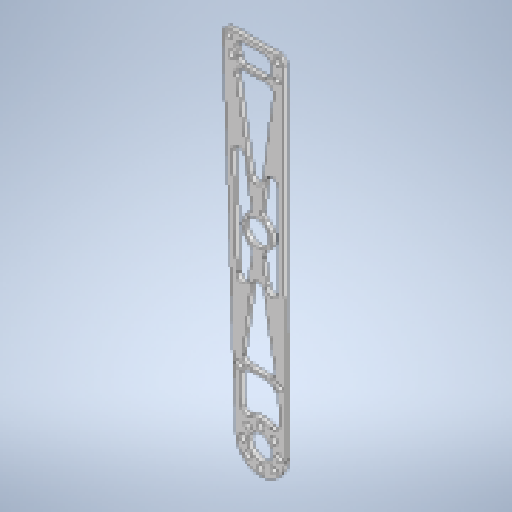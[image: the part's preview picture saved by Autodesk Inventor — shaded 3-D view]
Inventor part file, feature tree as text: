
AUTODESK INVENTOR PART (.ipt)
format: ipt  version: 2025.1 (Build 291241000, 241)  size: 314,880 bytes
history: native  units: mm
features: reference x12, other x8, extrude x2, fillet x2, sketch x2
ambient origin geometry x8: Origin, YZ Plane, XZ Plane, XY Plane, X Axis, Y Axis, Z Axis, Center Point
bodies: Body1 (feature_tree)
feature tree (26):
  other  "ソリッド1"
  extrude  "押し出し1"  Depth=8.0mm
  fillet  "フィレット1"  Radius=16.0mm
  extrude  "押し出し2"  Depth=12.0mm
  fillet  "フィレット2"  Radius=2.2mm
  sketch  "スケッチ1"
  reference  "参照1"
  other  "スケッチ円形状パターン1"
  reference  "参照2"
  reference  "参照3"
  reference  "参照4"
  reference  "参照5"
  reference  "参照6"
  reference  "参照7"
  reference  "参照8"
  reference  "参照9"
  reference  "参照10"
  reference  "参照11"
  reference  "参照12"
  sketch  "スケッチ2"
  other  "<userpath>\Documents\Inventor\Vixen\doutai.iam"
  other  "doutai.iam"
  other  "02157_SmallDiameterHornB_MIR1:1"
  other  "newnewude:1"
  other  "KRS2500_scale:15"
  other  "newnewude_2:1"
